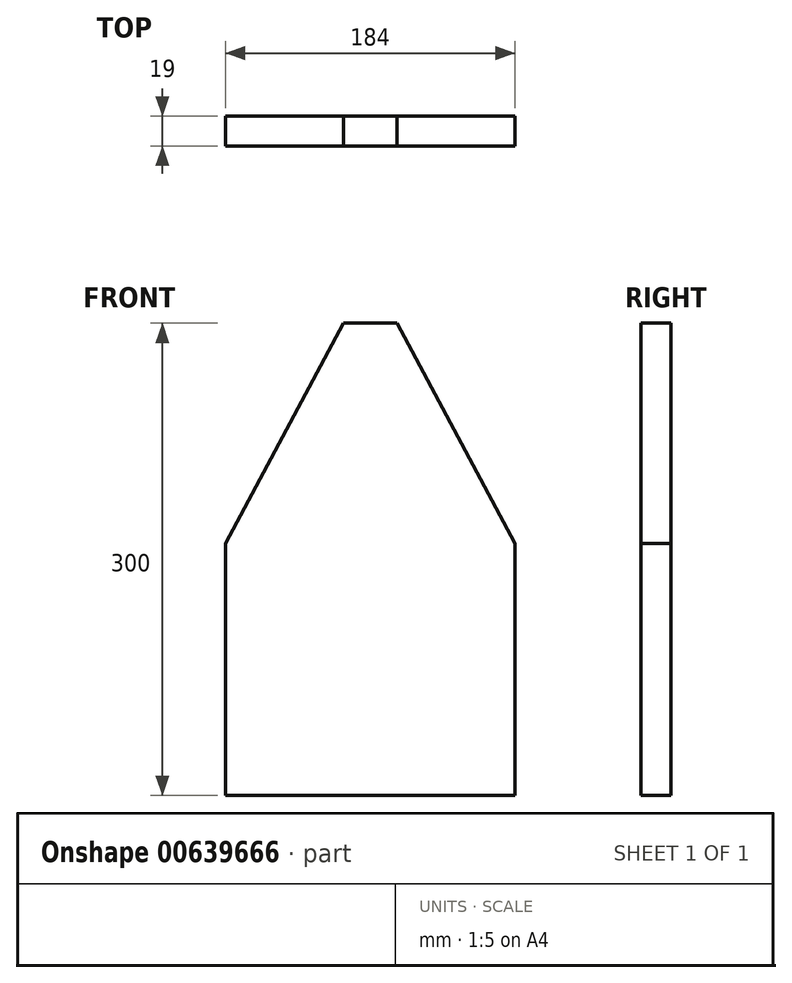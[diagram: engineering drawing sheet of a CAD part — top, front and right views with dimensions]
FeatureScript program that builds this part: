
annotation { "Feature Type Name" : "Feature", "Feature Type Description" : "" }
export const myFeature = defineFeature(function(context is Context, id is Id, definition is map)
    precondition{}
    {
        {
            var Q0;
            Q0=qCreatedBy(makeId("Front.planeOp"),FACE);
            var sketch = newSketch(context, id + "F0", { "sketchPlane" : qUnion([Q0])});
            skLineSegment(sketch, "E0.bottom", {"start": v(92, 150) * mm, "end": v(-92, 150) * mm});
            skLineSegment(sketch, "E0.top", {"start": v(92, -150) * mm, "end": v(-92, -150) * mm});
            skLineSegment(sketch, "E0.left", {"start": v(92, 150) * mm, "end": v(92, -150) * mm});
            skLineSegment(sketch, "E0.right", {"start": v(-92, 150) * mm, "end": v(-92, -150) * mm});
            skPoint(sketch, "E0.middle", {"position": v(0, 0) * mm});
            skSolve(sketch);
        }
        {
            var Q0;
            Q0 = qSketchRegion(id + "F0", true);
            extrude(context, id + "F1", {"entities" : qUnion([Q0]), "depth" : 19 * mm, "offsetDistance" : 25 * mm});
        }
        {
            var Q0;
            Q0=makeQuery(id+"F1.opExtrude","SWEPT_EDGE",EDGE,{"disambiguationData":[OSD([sQuery(id+"F0.wireOp",EDGE,"E0.bottom"),sQuery(id+"F0.wireOp",EDGE,"E0.left")])]});
            var Q1;
            Q1=makeQuery(id+"F1.opExtrude","SWEPT_EDGE",EDGE,{"disambiguationData":[OSD([sQuery(id+"F0.wireOp",EDGE,"E0.bottom"),sQuery(id+"F0.wireOp",EDGE,"E0.right")])]});
            chamfer(context, id + "F2", {"entities" : qUnion([Q0, Q1]), "chamferType" : ChamferType.TWO_OFFSETS, "width1" : 75 * mm, "oppositeDirection" : false, "width2" : 140 * mm, "tangentPropagation" : true});
        }
    });
